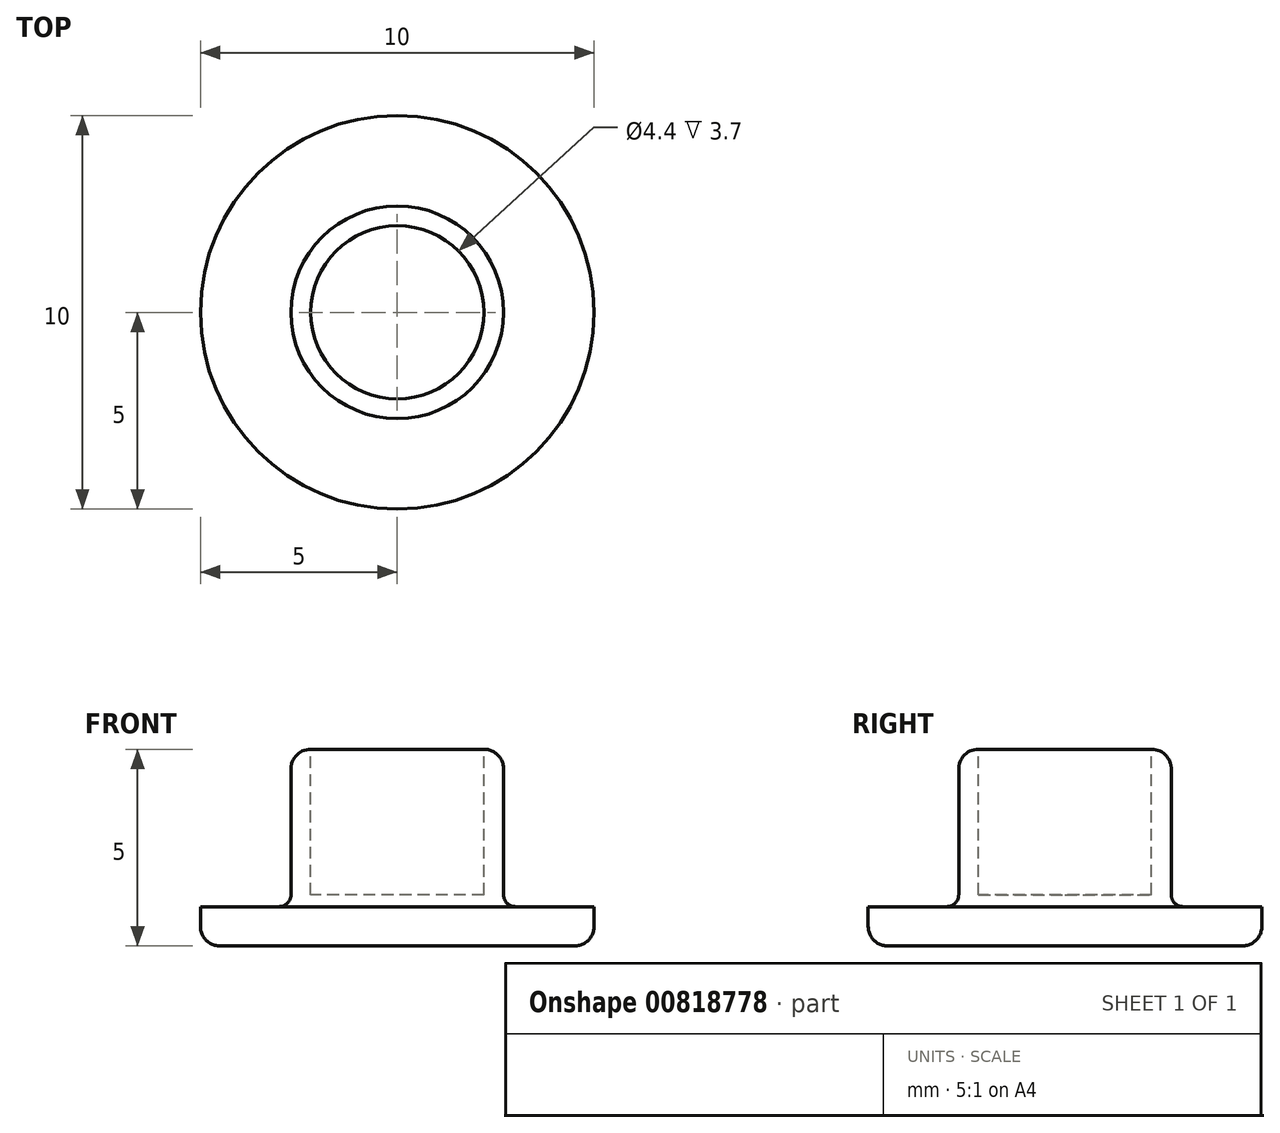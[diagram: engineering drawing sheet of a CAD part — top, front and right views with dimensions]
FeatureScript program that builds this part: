
annotation { "Feature Type Name" : "Feature", "Feature Type Description" : "" }
export const myFeature = defineFeature(function(context is Context, id is Id, definition is map)
    precondition{}
    {
        {
            var Q0;
            Q0=qCreatedBy(makeId("Front.planeOp"),FACE);
            var sketch = newSketch(context, id + "F0", { "sketchPlane" : qUnion([Q0])});
            skLineSegment(sketch, "E0.bottom", {"start": v(-5, 1) * mm, "end": v(0, 1) * mm});
            skLineSegment(sketch, "E0.top", {"start": v(-5, 0) * mm, "end": v(0, 0) * mm});
            skLineSegment(sketch, "E0.left", {"start": v(-5, 1) * mm, "end": v(-5, 0) * mm});
            skLineSegment(sketch, "E0.right", {"start": v(0, 1) * mm, "end": v(0, 0) * mm});
            skLineSegment(sketch, "E1.bottom", {"start": v(-2.2, 1) * mm, "end": v(-2.7, 1) * mm});
            skLineSegment(sketch, "E1.top", {"start": v(-2.2, 5) * mm, "end": v(-2.7, 5) * mm});
            skLineSegment(sketch, "E1.left", {"start": v(-2.7, 1) * mm, "end": v(-2.7, 5) * mm});
            skLineSegment(sketch, "E1.right", {"start": v(-2.2, 1) * mm, "end": v(-2.2, 5) * mm});
            skArc(sketch, "E2", {"start": v(-2.2, 3.7) * mm, "mid": v(-1.55, 3.05) * mm, "end": v(-2.2, 2.4) * mm});
            skLineSegment(sketch, "E3.bottom", {"start": v(0, 1) * mm, "end": v(-2.2, 1) * mm});
            skLineSegment(sketch, "E3.top", {"start": v(0, 1.3) * mm, "end": v(-2.2, 1.3) * mm});
            skLineSegment(sketch, "E3.left", {"start": v(0, 1) * mm, "end": v(0, 1.3) * mm});
            skLineSegment(sketch, "E3.right", {"start": v(-2.2, 1) * mm, "end": v(-2.2, 1.3) * mm});
            skSolve(sketch);
        }
        {
            var Q0;
            Q0=makeQuery(id+"F0.imprint","IMPRINT",FACE,{"disambiguationData":[TD([[makeQuery(id+"F0.imprint","IMPRINT",EDGE,{"derivedFrom":sQuery(id+"F0.wireOp",EDGE,"E0.top")}),1.0]])]});
            var Q1;
            {var subQ1=sQuery(id+"F0.wireOp",EDGE,"E1.top");Q1=makeQuery(id+"F0.imprint","IMPRINT",FACE,{"disambiguationData":[TD([[makeQuery(id+"F0.imprint","IMPRINT",EDGE,{"derivedFrom":subQ1}),1.0]])]});}
            var Q2;
            {var subQ0=sQuery(id+"F0.wireOp",EDGE,"E2");Q2=makeQuery(id+"F0.imprint","IMPRINT",FACE,{"disambiguationData":[TD([[makeQuery(id+"F0.imprint","IMPRINT",EDGE,{"derivedFrom":subQ0}),-1.0]])]});}
            var Q3;
            {var subQ4=sQuery(id+"F0.wireOp",EDGE,"E3.top");Q3=makeQuery(id+"F0.imprint","IMPRINT",FACE,{"disambiguationData":[TD([[makeQuery(id+"F0.imprint","IMPRINT",EDGE,{"derivedFrom":subQ4}),1.0]])]});}
            var Q4;
            Q4=sQuery(id+"F0.wireOp",EDGE,"E0.right");
            revolve(context, id + "F1", {"surfaceOperationType" : NewSurfaceOperationType.NEW, "entities" : qUnion([Q0, Q1, Q2, Q3]), "axis" : qUnion([Q4]), "revolveType" : RevolveType.FULL});
        }
        {
            var Q0;
            Q0=makeQuery(id+"F1.opRevolve","SWEPT_EDGE",EDGE,{"disambiguationData":[OSD([sQuery(id+"F0.wireOp",EDGE,"E1.top"),sQuery(id+"F0.wireOp",EDGE,"E1.left")])]});
            var Q1;
            Q1=makeQuery(id+"F1.opRevolve","SWEPT_EDGE",EDGE,{"disambiguationData":[OSD([sQuery(id+"F0.wireOp",EDGE,"E0.top"),sQuery(id+"F0.wireOp",EDGE,"E0.left")])]});
            fillet(context, id + "F2", {"entities" : qUnion([Q0, Q1]), "radius" : 0.5 * mm, "tangentPropagation" : true, "allowEdgeOverflow" : false});
        }
        {
            var Q0;
            Q0=makeQuery(id+"F1.opRevolve","SWEPT_EDGE",EDGE,{"disambiguationData":[OSD([sQuery(id+"F0.wireOp",EDGE,"E0.bottom"),sQuery(id+"F0.wireOp",EDGE,"E1.left")])]});
            fillet(context, id + "F3", {"entities" : qUnion([Q0]), "radius" : 0.3 * mm, "tangentPropagation" : true, "allowEdgeOverflow" : false});
        }
    });
